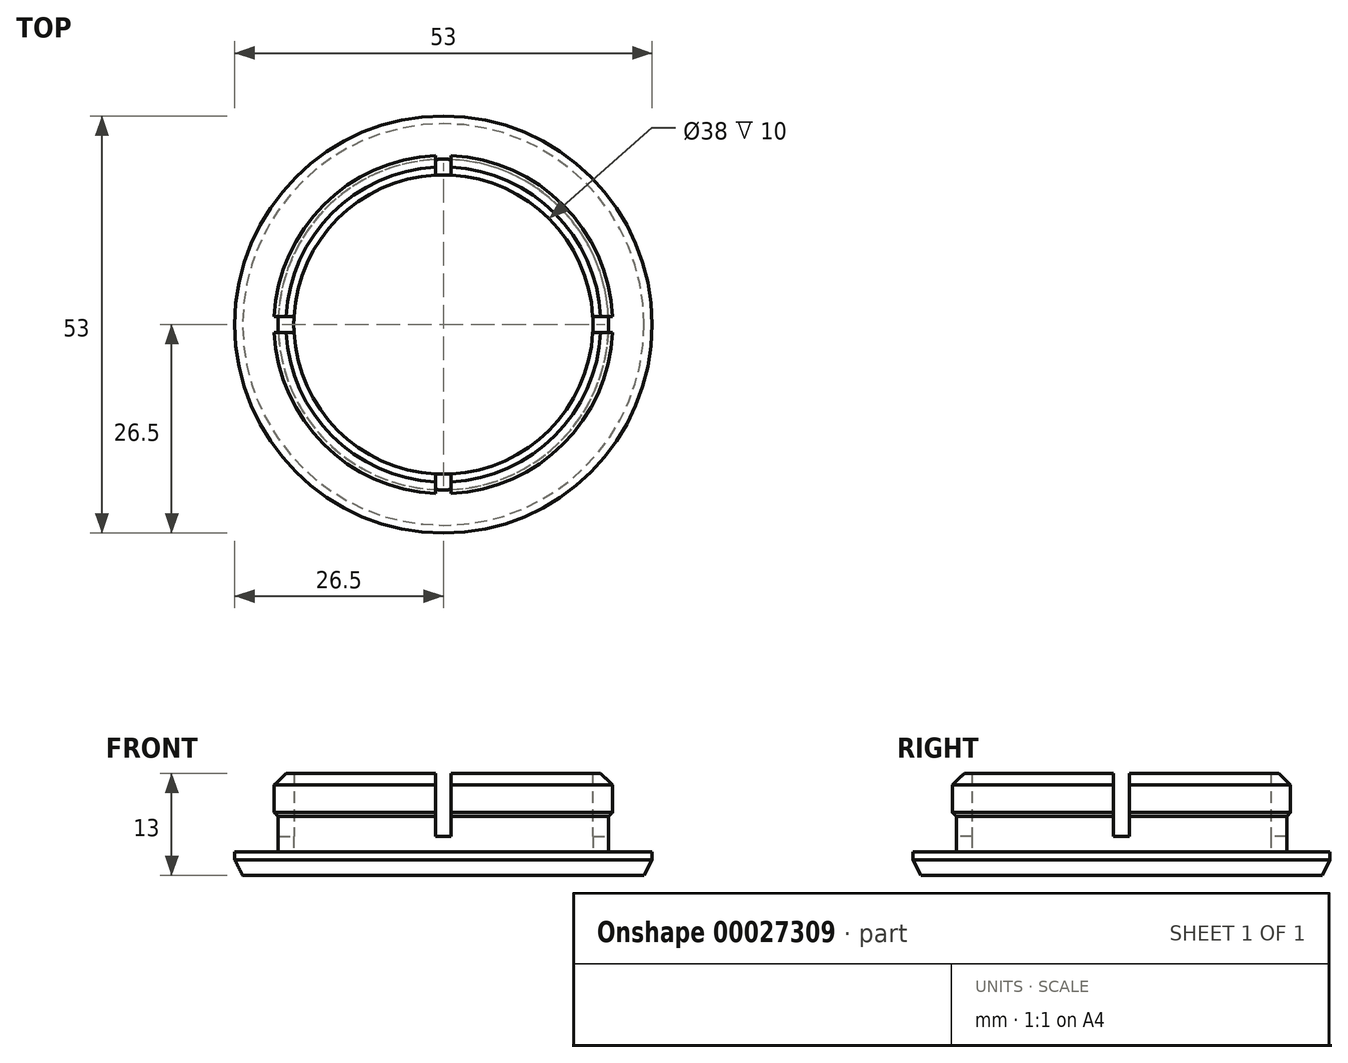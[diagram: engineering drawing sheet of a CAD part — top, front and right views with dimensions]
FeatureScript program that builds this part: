
annotation { "Feature Type Name" : "Feature", "Feature Type Description" : "" }
export const myFeature = defineFeature(function(context is Context, id is Id, definition is map)
    precondition{}
    {
        {
            var Q0;
            Q0=qCreatedBy(makeId("Top.planeOp"),FACE);
            var sketch = newSketch(context, id + "F0", { "sketchPlane" : qUnion([Q0])});
            skCircle(sketch, "E0", {"center": v(0, 0) * mm, "radius": 19 * mm});
            skCircle(sketch, "E1", {"center": v(0, 0) * mm, "radius": 21 * mm});
            skSolve(sketch);
        }
        {
            var Q0;
            Q0=qSketchRegion(id+"F0",true);
            extrude(context, id + "F1", {"entities" : qUnion([Q0]), "depth" : 10 * mm});
        }
        {
            var Q0;
            Q0=makeQuery(id+"F1.opExtrude","CAP_FACE",FACE,{"disambiguationData":[OSD([sQuery(id+"F0.wireOp",EDGE,"E0"),sQuery(id+"F0.wireOp",EDGE,"E1")])],"isStart":false});
            var sketch = newSketch(context, id + "F2", { "sketchPlane" : qUnion([Q0])});
            skCircle(sketch, "E2", {"center": v(0, 0) * mm, "radius": 19 * mm});
            skCircle(sketch, "E3", {"center": v(0, 0) * mm, "radius": 21.5 * mm});
            skSolve(sketch);
        }
        {
            var Q0;
            Q0=qSketchRegion(id+"F2",true);
            extrude(context, id + "F3", {"entities" : qUnion([Q0]), "operationType" : NewBodyOperationType.ADD, "oppositeDirection" : true, "depth" : 5 * mm});
        }
        {
            var Q0;
            Q0=makeQuery(id+"F3.opExtrude","CAP_EDGE",EDGE,{"disambiguationData":[OSD([sQuery(id+"F2.wireOp",EDGE,"E3")])],"isStart":true});
            chamfer(context, id + "F4", {"entities" : qUnion([Q0]), "width" : 1.5 * mm, "tangentPropagation" : true});
        }
        {
            var Q0;
            Q0=makeQuery(id+"F3.boolean.opBoolean","MERGE",FACE,{"derivedFrom":[makeQuery(id+"F1.opExtrude","CAP_FACE",FACE,{"disambiguationData":[OSD([sQuery(id+"F0.wireOp",EDGE,"E0"),sQuery(id+"F0.wireOp",EDGE,"E1")])],"isStart":false}),makeQuery(id+"F3.opExtrude","CAP_FACE",FACE,{"disambiguationData":[OSD([sQuery(id+"F2.wireOp",EDGE,"E2"),sQuery(id+"F2.wireOp",EDGE,"E3")])],"isStart":true})]});
            var sketch = newSketch(context, id + "F5", { "sketchPlane" : qUnion([Q0])});
            skLineSegment(sketch, "E4.bottom", {"start": v(-1, 25) * mm, "end": v(1, 25) * mm});
            skLineSegment(sketch, "E4.top", {"start": v(-1, -25) * mm, "end": v(1, -25) * mm});
            skLineSegment(sketch, "E4.left", {"start": v(-1, 25) * mm, "end": v(-1, -25) * mm});
            skLineSegment(sketch, "E4.right", {"start": v(1, 25) * mm, "end": v(1, -25) * mm});
            skLineSegment(sketch, "E5.bottom", {"start": v(-25, 1) * mm, "end": v(25, 1) * mm});
            skLineSegment(sketch, "E5.top", {"start": v(-25, -1) * mm, "end": v(25, -1) * mm});
            skLineSegment(sketch, "E5.left", {"start": v(-25, 1) * mm, "end": v(-25, -1) * mm});
            skLineSegment(sketch, "E5.right", {"start": v(25, 1) * mm, "end": v(25, -1) * mm});
            skSolve(sketch);
        }
        {
            var Q0;
            Q0=qSketchRegion(id+"F5",true);
            extrude(context, id + "F6", {"entities" : qUnion([Q0]), "operationType" : NewBodyOperationType.REMOVE, "oppositeDirection" : true, "depth" : 8 * mm});
        }
        {
            var Q0;
            Q0=makeQuery(id+"F1.opExtrude","CAP_FACE",FACE,{"disambiguationData":[OSD([sQuery(id+"F0.wireOp",EDGE,"E0"),sQuery(id+"F0.wireOp",EDGE,"E1")])],"isStart":true});
            var sketch = newSketch(context, id + "F7", { "sketchPlane" : qUnion([Q0])});
            skCircle(sketch, "E6", {"center": v(0, 0) * mm, "radius": 26.5 * mm});
            skSolve(sketch);
        }
        {
            var Q0;
            Q0=qSketchRegion(id+"F7",true);
            extrude(context, id + "F8", {"entities" : qUnion([Q0]), "operationType" : NewBodyOperationType.ADD, "depth" : 3 * mm});
        }
        {
            var Q0;
            Q0=makeQuery(id+"F8.opExtrude","CAP_EDGE",EDGE,{"disambiguationData":[OSD([sQuery(id+"F7.wireOp",EDGE,"E6")])],"isStart":false});
            chamfer(context, id + "F9", {"entities" : qUnion([Q0]), "chamferType" : ChamferType.TWO_OFFSETS, "width1" : 1 * mm, "oppositeDirection" : false, "width2" : 2 * mm, "tangentPropagation" : true});
        }
        {
            var Q0;
            {var subQ0=sQuery(id+"F0.wireOp",EDGE,"E1");var subQ1=makeQuery(id+"F1.opExtrude","SWEPT_FACE",FACE,{"disambiguationData":[OSD([subQ0])]});var subQ2=sQuery(id+"F2.wireOp",EDGE,"E2");var subQ3=sQuery(id+"F2.wireOp",EDGE,"E3");var subQ4=makeQuery(id+"F3.opExtrude","CAP_FACE",FACE,{"disambiguationData":[OSD([subQ2,subQ3])],"isStart":false});var subQ5=sQuery(id+"F5.wireOp",EDGE,"E5.top");var subQ6=sQuery(id+"F0.wireOp",EDGE,"E0");var subQ7=makeQuery(id+"F1.opExtrude","CAP_EDGE",EDGE,{"disambiguationData":[OSD([subQ6])],"isStart":false});var subQ9=sQuery(id+"F5.wireOp",EDGE,"E4.right");var subQ10=makeQuery(id+"F5.imprint","INTERSECT",VERTEX,{"derivedFrom":[subQ9,subQ5]});var subQ13=makeQuery(id+"F5.imprint","INTERSECT",VERTEX,{"disambiguationData":[OD(1.0)],"derivedFrom":[subQ7,subQ9]});Q0=makeQuery(id+"F6.boolean.opBoolean","SPLIT",EDGE,{"disambiguationData":[TD([makeQuery(id+"F6.opExtrude","SWEPT_FACE",FACE,{"disambiguationData":[OSD([subQ9]),TDD([makeQuery(id+"F5.imprint","IMPRINT",EDGE,{"disambiguationData":[TD([[subQ10,-1.0]])],"derivedFrom":subQ9}),makeQuery(id+"F5.imprint","IMPRINT",EDGE,{"disambiguationData":[TD([[subQ13,-1.0]])],"derivedFrom":subQ9}),makeQuery(id+"F5.imprint","IMPRINT",EDGE,{"disambiguationData":[TD([[makeQuery(id+"F5.imprint","INTERSECT",VERTEX,{"derivedFrom":[sQuery(id+"F5.wireOp",EDGE,"E4.top"),subQ9]}),1.0]])],"derivedFrom":subQ9})])]})])],"derivedFrom":makeQuery(id+"F3.boolean.opBoolean","INTERSECT",EDGE,{"derivedFrom":[subQ1,subQ4]})});}
            var Q1;
            {var subQ0=sQuery(id+"F0.wireOp",EDGE,"E1");var subQ1=makeQuery(id+"F1.opExtrude","SWEPT_FACE",FACE,{"disambiguationData":[OSD([subQ0])]});var subQ2=sQuery(id+"F2.wireOp",EDGE,"E2");var subQ3=sQuery(id+"F2.wireOp",EDGE,"E3");var subQ4=makeQuery(id+"F3.opExtrude","CAP_FACE",FACE,{"disambiguationData":[OSD([subQ2,subQ3])],"isStart":false});var subQ5=sQuery(id+"F5.wireOp",EDGE,"E5.bottom");var subQ6=sQuery(id+"F0.wireOp",EDGE,"E0");var subQ7=makeQuery(id+"F1.opExtrude","CAP_EDGE",EDGE,{"disambiguationData":[OSD([subQ6])],"isStart":false});var subQ9=sQuery(id+"F5.wireOp",EDGE,"E4.right");var subQ10=makeQuery(id+"F5.imprint","INTERSECT",VERTEX,{"derivedFrom":[subQ9,subQ5]});var subQ14=makeQuery(id+"F5.imprint","INTERSECT",VERTEX,{"disambiguationData":[OD(0.0)],"derivedFrom":[subQ7,subQ9]});Q1=makeQuery(id+"F6.boolean.opBoolean","SPLIT",EDGE,{"disambiguationData":[TD([makeQuery(id+"F6.opExtrude","SWEPT_FACE",FACE,{"disambiguationData":[OSD([subQ9]),TDD([makeQuery(id+"F5.imprint","IMPRINT",EDGE,{"disambiguationData":[TD([[makeQuery(id+"F5.imprint","INTERSECT",VERTEX,{"derivedFrom":[sQuery(id+"F5.wireOp",EDGE,"E4.bottom"),subQ9]}),-1.0]])],"derivedFrom":subQ9}),makeQuery(id+"F5.imprint","IMPRINT",EDGE,{"disambiguationData":[TD([[subQ14,1.0]])],"derivedFrom":subQ9}),makeQuery(id+"F5.imprint","IMPRINT",EDGE,{"disambiguationData":[TD([[subQ10,1.0]])],"derivedFrom":subQ9})])]})])],"derivedFrom":makeQuery(id+"F3.boolean.opBoolean","INTERSECT",EDGE,{"derivedFrom":[subQ1,subQ4]})});}
            var Q2;
            {var subQ0=sQuery(id+"F0.wireOp",EDGE,"E1");var subQ1=makeQuery(id+"F1.opExtrude","SWEPT_FACE",FACE,{"disambiguationData":[OSD([subQ0])]});var subQ2=sQuery(id+"F2.wireOp",EDGE,"E2");var subQ3=sQuery(id+"F2.wireOp",EDGE,"E3");var subQ4=makeQuery(id+"F3.opExtrude","CAP_FACE",FACE,{"disambiguationData":[OSD([subQ2,subQ3])],"isStart":false});var subQ5=sQuery(id+"F5.wireOp",EDGE,"E5.top");var subQ6=sQuery(id+"F0.wireOp",EDGE,"E0");var subQ9=makeQuery(id+"F1.opExtrude","CAP_EDGE",EDGE,{"disambiguationData":[OSD([subQ6])],"isStart":false});var subQ11=sQuery(id+"F5.wireOp",EDGE,"E4.left");var subQ12=makeQuery(id+"F5.imprint","INTERSECT",VERTEX,{"derivedFrom":[subQ11,subQ5]});var subQ13=makeQuery(id+"F5.imprint","INTERSECT",VERTEX,{"disambiguationData":[OD(1.0)],"derivedFrom":[subQ9,subQ11]});Q2=makeQuery(id+"F6.boolean.opBoolean","SPLIT",EDGE,{"disambiguationData":[TD([makeQuery(id+"F6.opExtrude","SWEPT_FACE",FACE,{"disambiguationData":[OSD([subQ11]),TDD([makeQuery(id+"F5.imprint","IMPRINT",EDGE,{"disambiguationData":[TD([[subQ12,-1.0]])],"derivedFrom":subQ11}),makeQuery(id+"F5.imprint","IMPRINT",EDGE,{"disambiguationData":[TD([[subQ13,-1.0]])],"derivedFrom":subQ11}),makeQuery(id+"F5.imprint","IMPRINT",EDGE,{"disambiguationData":[TD([[makeQuery(id+"F5.imprint","INTERSECT",VERTEX,{"derivedFrom":[sQuery(id+"F5.wireOp",EDGE,"E4.top"),subQ11]}),1.0]])],"derivedFrom":subQ11})])]})])],"derivedFrom":makeQuery(id+"F3.boolean.opBoolean","INTERSECT",EDGE,{"derivedFrom":[subQ1,subQ4]})});}
            var Q3;
            {var subQ0=sQuery(id+"F0.wireOp",EDGE,"E1");var subQ1=makeQuery(id+"F1.opExtrude","SWEPT_FACE",FACE,{"disambiguationData":[OSD([subQ0])]});var subQ2=sQuery(id+"F2.wireOp",EDGE,"E2");var subQ3=sQuery(id+"F2.wireOp",EDGE,"E3");var subQ4=makeQuery(id+"F3.opExtrude","CAP_FACE",FACE,{"disambiguationData":[OSD([subQ2,subQ3])],"isStart":false});var subQ5=sQuery(id+"F5.wireOp",EDGE,"E5.bottom");var subQ6=sQuery(id+"F0.wireOp",EDGE,"E0");var subQ9=makeQuery(id+"F1.opExtrude","CAP_EDGE",EDGE,{"disambiguationData":[OSD([subQ6])],"isStart":false});var subQ11=sQuery(id+"F5.wireOp",EDGE,"E4.left");var subQ12=makeQuery(id+"F5.imprint","INTERSECT",VERTEX,{"derivedFrom":[subQ11,subQ5]});var subQ14=makeQuery(id+"F5.imprint","INTERSECT",VERTEX,{"disambiguationData":[OD(0.0)],"derivedFrom":[subQ9,subQ11]});Q3=makeQuery(id+"F6.boolean.opBoolean","SPLIT",EDGE,{"disambiguationData":[TD([makeQuery(id+"F6.opExtrude","SWEPT_FACE",FACE,{"disambiguationData":[OSD([subQ11]),TDD([makeQuery(id+"F5.imprint","IMPRINT",EDGE,{"disambiguationData":[TD([[makeQuery(id+"F5.imprint","INTERSECT",VERTEX,{"derivedFrom":[sQuery(id+"F5.wireOp",EDGE,"E4.bottom"),subQ11]}),-1.0]])],"derivedFrom":subQ11}),makeQuery(id+"F5.imprint","IMPRINT",EDGE,{"disambiguationData":[TD([[subQ14,1.0]])],"derivedFrom":subQ11}),makeQuery(id+"F5.imprint","IMPRINT",EDGE,{"disambiguationData":[TD([[subQ12,1.0]])],"derivedFrom":subQ11})])]})])],"derivedFrom":makeQuery(id+"F3.boolean.opBoolean","INTERSECT",EDGE,{"derivedFrom":[subQ1,subQ4]})});}
            chamfer(context, id + "F10", {"entities" : qUnion([Q0, Q1, Q2, Q3]), "width" : .5 * mm, "tangentPropagation" : true});
        }
    });
